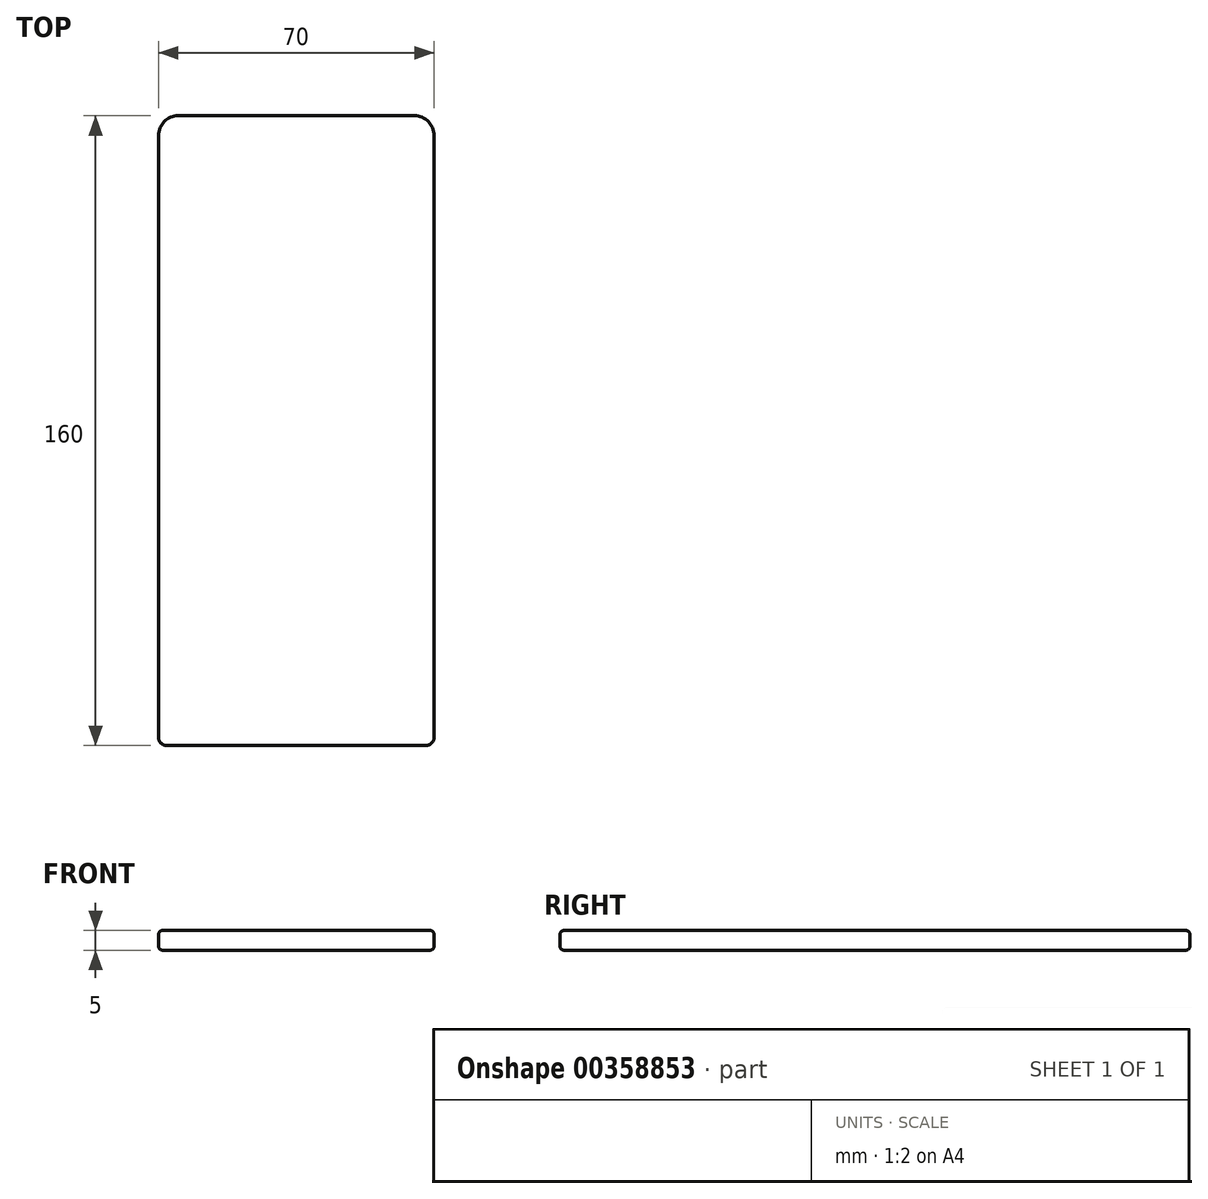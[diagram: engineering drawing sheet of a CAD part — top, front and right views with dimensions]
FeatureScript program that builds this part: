
annotation { "Feature Type Name" : "Feature", "Feature Type Description" : "" }
export const myFeature = defineFeature(function(context is Context, id is Id, definition is map)
    precondition{}
    {
        {
            var Q0;
            Q0=qCreatedBy(makeId("Top.planeOp"),FACE);
            var sketch = newSketch(context, id + "F0", { "sketchPlane" : qUnion([Q0])});
            skLineSegment(sketch, "E0.bottom", {"start": v(-30, 80) * mm, "end": v(30, 80) * mm});
            skLineSegment(sketch, "E0.top", {"start": v(-33, -80) * mm, "end": v(33, -80) * mm});
            skLineSegment(sketch, "E0.left", {"start": v(-35, 75) * mm, "end": v(-35, -78) * mm});
            skLineSegment(sketch, "E0.right", {"start": v(35, 75) * mm, "end": v(35, -78) * mm});
            skPoint(sketch, "E0.middle", {"position": v(0, 0) * mm});
            skPoint(sketch, "E1.visualSharp", {"position": v(-35, 80) * mm});
            skArc(sketch, "E1.filletArc", {"start": v(-30, 80) * mm, "mid": v(-33.54, 78.54) * mm, "end": v(-35, 75) * mm});
            skPoint(sketch, "E2.visualSharp", {"position": v(35, 80) * mm});
            skArc(sketch, "E2.filletArc", {"start": v(35, 75) * mm, "mid": v(33.54, 78.54) * mm, "end": v(30, 80) * mm});
            skPoint(sketch, "E3.visualSharp", {"position": v(35, -80) * mm});
            skArc(sketch, "E3.filletArc", {"start": v(33, -80) * mm, "mid": v(34.41, -79.41) * mm, "end": v(35, -78) * mm});
            skPoint(sketch, "E4.visualSharp", {"position": v(-35, -80) * mm});
            skArc(sketch, "E4.filletArc", {"start": v(-35, -78) * mm, "mid": v(-34.41, -79.41) * mm, "end": v(-33, -80) * mm});
            skSolve(sketch);
        }
        {
            var Q0;
            Q0=makeQuery(id+"F0.imprint","IMPRINT",FACE,{"disambiguationData":[TD([[makeQuery(id+"F0.imprint","IMPRINT",EDGE,{"derivedFrom":sQuery(id+"F0.wireOp",EDGE,"E0.bottom")}),-1.0]])]});
            extrude(context, id + "F1", {"entities" : qUnion([Q0]), "endBound" : BoundingType.SYMMETRIC, "depth" : 5 * mm});
        }
        {
            var Q0;
            Q0=makeQuery(id+"F1.opExtrude","CAP_FACE",FACE,{"disambiguationData":[OSD([sQuery(id+"F0.wireOp",EDGE,"E0.bottom"),sQuery(id+"F0.wireOp",EDGE,"E0.top"),sQuery(id+"F0.wireOp",EDGE,"E0.left"),sQuery(id+"F0.wireOp",EDGE,"E0.right"),sQuery(id+"F0.wireOp",EDGE,"E1.filletArc"),sQuery(id+"F0.wireOp",EDGE,"E2.filletArc"),sQuery(id+"F0.wireOp",EDGE,"E3.filletArc"),sQuery(id+"F0.wireOp",EDGE,"E4.filletArc")])],"isStart":true});
            var Q1;
            Q1=makeQuery(id+"F1.opExtrude","CAP_FACE",FACE,{"disambiguationData":[OSD([sQuery(id+"F0.wireOp",EDGE,"E0.bottom"),sQuery(id+"F0.wireOp",EDGE,"E0.top"),sQuery(id+"F0.wireOp",EDGE,"E0.left"),sQuery(id+"F0.wireOp",EDGE,"E0.right"),sQuery(id+"F0.wireOp",EDGE,"E1.filletArc"),sQuery(id+"F0.wireOp",EDGE,"E2.filletArc"),sQuery(id+"F0.wireOp",EDGE,"E3.filletArc"),sQuery(id+"F0.wireOp",EDGE,"E4.filletArc")])],"isStart":false});
            fillet(context, id + "F2", {"entities" : qUnion([Q0, Q1]), "radius" : 1 * mm, "tangentPropagation" : true, "allowEdgeOverflow" : false});
        }
    });
